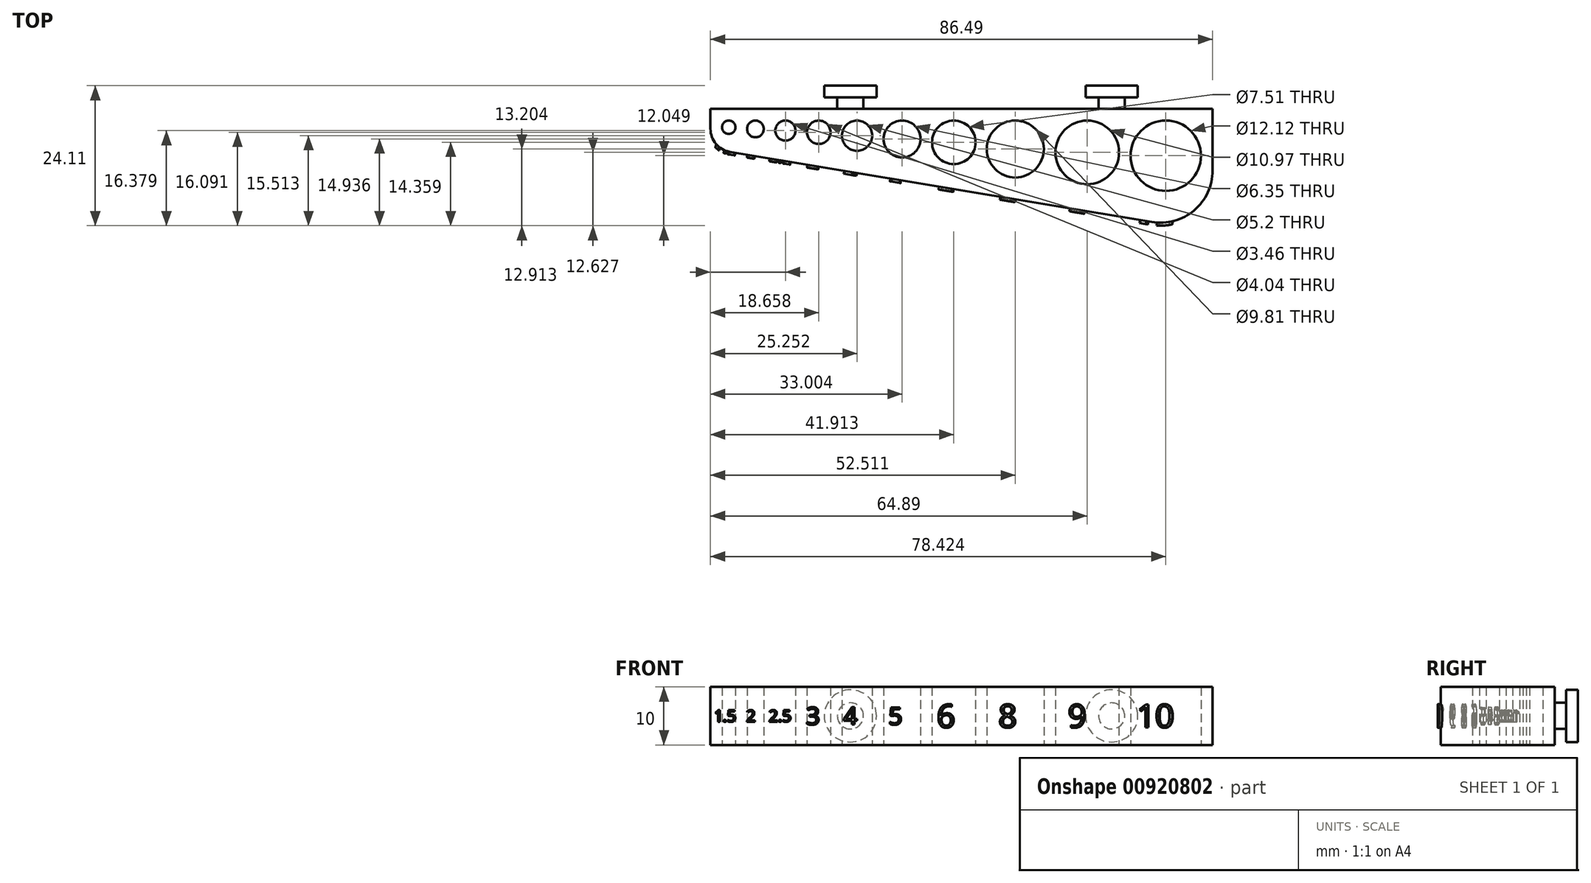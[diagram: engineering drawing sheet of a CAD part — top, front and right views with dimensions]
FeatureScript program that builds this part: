
annotation { "Feature Type Name" : "Feature", "Feature Type Description" : "" }
export const myFeature = defineFeature(function(context is Context, id is Id, definition is map)
    precondition{}
    {
        {
            var Q0;
            Q0=qCreatedBy(makeId("Top.planeOp"),FACE);
            var sketch = newSketch(context, id + "F0", { "sketchPlane" : qUnion([Q0])});
            skCircle(sketch, "E0.cCircle", {"center": v(30.9, 21.07) * mm, "radius": 4.25 * mm, "construction": true});
            skLineSegment(sketch, "E0.0", {"start": v(35.4, 19.12) * mm, "end": v(31.46, 16.2) * mm, "construction": true});
            skLineSegment(sketch, "E0.1", {"start": v(31.46, 16.2) * mm, "end": v(26.96, 18.15) * mm, "construction": true});
            skLineSegment(sketch, "E0.2", {"start": v(26.96, 18.15) * mm, "end": v(26.4, 23.03) * mm, "construction": true});
            skLineSegment(sketch, "E0.3", {"start": v(26.4, 23.03) * mm, "end": v(30.35, 25.95) * mm, "construction": true});
            skLineSegment(sketch, "E0.4", {"start": v(30.35, 25.95) * mm, "end": v(34.85, 24) * mm, "construction": true});
            skLineSegment(sketch, "E0.5", {"start": v(34.85, 24) * mm, "end": v(35.4, 19.12) * mm, "construction": true});
            skPoint(sketch, "E0.0.midPoint", {"position": v(33.43, 17.66) * mm});
            skCircle(sketch, "E1", {"center": v(30.9, 21.07) * mm, "radius": 4.9 * mm});
            skCircle(sketch, "E2.cCircle", {"center": v(-2.95, 23.96) * mm, "radius": 1.75 * mm, "construction": true});
            skLineSegment(sketch, "E2.0", {"start": v(-1.1, 23.15) * mm, "end": v(-2.72, 21.95) * mm, "construction": true});
            skLineSegment(sketch, "E2.1", {"start": v(-2.72, 21.95) * mm, "end": v(-4.58, 22.76) * mm, "construction": true});
            skLineSegment(sketch, "E2.2", {"start": v(-4.58, 22.76) * mm, "end": v(-4.8, 24.77) * mm, "construction": true});
            skLineSegment(sketch, "E2.3", {"start": v(-4.8, 24.77) * mm, "end": v(-3.18, 25.97) * mm, "construction": true});
            skLineSegment(sketch, "E2.4", {"start": v(-3.18, 25.97) * mm, "end": v(-1.33, 25.16) * mm, "construction": true});
            skLineSegment(sketch, "E2.5", {"start": v(-1.33, 25.16) * mm, "end": v(-1.1, 23.15) * mm, "construction": true});
            skPoint(sketch, "E2.0.midPoint", {"position": v(-1.91, 22.55) * mm});
            skCircle(sketch, "E3", {"center": v(-2.95, 23.96) * mm, "radius": 2.02 * mm});
            skCircle(sketch, "E4.cCircle", {"center": v(-8.7, 24.25) * mm, "radius": 1.5 * mm, "construction": true});
            skLineSegment(sketch, "E4.0", {"start": v(-7.1, 23.56) * mm, "end": v(-8.5, 22.53) * mm, "construction": true});
            skLineSegment(sketch, "E4.1", {"start": v(-8.5, 22.53) * mm, "end": v(-10.09, 23.22) * mm, "construction": true});
            skLineSegment(sketch, "E4.2", {"start": v(-10.09, 23.22) * mm, "end": v(-10.29, 24.94) * mm, "construction": true});
            skLineSegment(sketch, "E4.3", {"start": v(-10.29, 24.94) * mm, "end": v(-8.9, 25.97) * mm, "construction": true});
            skLineSegment(sketch, "E4.4", {"start": v(-8.9, 25.97) * mm, "end": v(-7.3, 25.28) * mm, "construction": true});
            skLineSegment(sketch, "E4.5", {"start": v(-7.3, 25.28) * mm, "end": v(-7.1, 23.56) * mm, "construction": true});
            skPoint(sketch, "E4.0.midPoint", {"position": v(-7.8, 23.04) * mm});
            skCircle(sketch, "E5", {"center": v(-8.7, 24.25) * mm, "radius": 1.73 * mm});
            skCircle(sketch, "E6.cCircle", {"center": v(-18.45, 24.83) * mm, "radius": 1 * mm, "construction": true});
            skLineSegment(sketch, "E6.0", {"start": v(-17.7, 23.95) * mm, "end": v(-18.84, 23.74) * mm, "construction": true});
            skLineSegment(sketch, "E6.1", {"start": v(-18.84, 23.74) * mm, "end": v(-19.59, 24.61) * mm, "construction": true});
            skLineSegment(sketch, "E6.2", {"start": v(-19.59, 24.61) * mm, "end": v(-19.2, 25.7) * mm, "construction": true});
            skLineSegment(sketch, "E6.3", {"start": v(-19.2, 25.7) * mm, "end": v(-18.07, 25.92) * mm, "construction": true});
            skLineSegment(sketch, "E6.4", {"start": v(-18.07, 25.92) * mm, "end": v(-17.32, 25.04) * mm, "construction": true});
            skLineSegment(sketch, "E6.5", {"start": v(-17.32, 25.04) * mm, "end": v(-17.7, 23.95) * mm, "construction": true});
            skPoint(sketch, "E6.0.midPoint", {"position": v(-18.27, 23.84) * mm});
            skCircle(sketch, "E7", {"center": v(-18.45, 24.83) * mm, "radius": 1.15 * mm});
            skCircle(sketch, "E8.cCircle", {"center": v(3.64, 23.38) * mm, "radius": 2.25 * mm, "construction": true});
            skLineSegment(sketch, "E8.0", {"start": v(6.02, 22.35) * mm, "end": v(3.94, 20.8) * mm, "construction": true});
            skLineSegment(sketch, "E8.1", {"start": v(3.94, 20.8) * mm, "end": v(1.55, 21.84) * mm, "construction": true});
            skLineSegment(sketch, "E8.2", {"start": v(1.55, 21.84) * mm, "end": v(1.26, 24.42) * mm, "construction": true});
            skLineSegment(sketch, "E8.3", {"start": v(1.26, 24.42) * mm, "end": v(3.35, 25.96) * mm, "construction": true});
            skLineSegment(sketch, "E8.4", {"start": v(3.35, 25.96) * mm, "end": v(5.73, 24.93) * mm, "construction": true});
            skLineSegment(sketch, "E8.5", {"start": v(5.73, 24.93) * mm, "end": v(6.02, 22.35) * mm, "construction": true});
            skPoint(sketch, "E8.0.midPoint", {"position": v(4.98, 21.57) * mm});
            skCircle(sketch, "E9", {"center": v(3.64, 23.38) * mm, "radius": 2.6 * mm});
            skCircle(sketch, "E10.cCircle", {"center": v(11.4, 22.8) * mm, "radius": 2.75 * mm, "construction": true});
            skLineSegment(sketch, "E10.0", {"start": v(14.3, 21.54) * mm, "end": v(11.75, 19.65) * mm, "construction": true});
            skLineSegment(sketch, "E10.1", {"start": v(11.75, 19.65) * mm, "end": v(8.84, 20.92) * mm, "construction": true});
            skLineSegment(sketch, "E10.2", {"start": v(8.84, 20.92) * mm, "end": v(8.48, 24.07) * mm, "construction": true});
            skLineSegment(sketch, "E10.3", {"start": v(8.48, 24.07) * mm, "end": v(11.03, 25.96) * mm, "construction": true});
            skLineSegment(sketch, "E10.4", {"start": v(11.03, 25.96) * mm, "end": v(13.95, 24.7) * mm, "construction": true});
            skLineSegment(sketch, "E10.5", {"start": v(13.95, 24.7) * mm, "end": v(14.3, 21.54) * mm, "construction": true});
            skPoint(sketch, "E10.0.midPoint", {"position": v(13.03, 20.6) * mm});
            skCircle(sketch, "E11", {"center": v(11.4, 22.8) * mm, "radius": 3.18 * mm});
            skCircle(sketch, "E12.cCircle", {"center": v(43.28, 20.5) * mm, "radius": 4.75 * mm, "construction": true});
            skLineSegment(sketch, "E12.0", {"start": v(48.3, 18.3) * mm, "end": v(43.9, 15.05) * mm, "construction": true});
            skLineSegment(sketch, "E12.1", {"start": v(43.9, 15.05) * mm, "end": v(38.87, 17.23) * mm, "construction": true});
            skLineSegment(sketch, "E12.2", {"start": v(38.87, 17.23) * mm, "end": v(38.25, 22.68) * mm, "construction": true});
            skLineSegment(sketch, "E12.3", {"start": v(38.25, 22.68) * mm, "end": v(42.66, 25.95) * mm, "construction": true});
            skLineSegment(sketch, "E12.4", {"start": v(42.66, 25.95) * mm, "end": v(47.69, 23.76) * mm, "construction": true});
            skLineSegment(sketch, "E12.5", {"start": v(47.69, 23.76) * mm, "end": v(48.3, 18.3) * mm, "construction": true});
            skPoint(sketch, "E12.0.midPoint", {"position": v(46.1, 16.68) * mm});
            skCircle(sketch, "E13", {"center": v(43.28, 20.5) * mm, "radius": 5.48 * mm});
            skCircle(sketch, "E14.cCircle", {"center": v(56.81, 19.92) * mm, "radius": 5.25 * mm, "construction": true});
            skLineSegment(sketch, "E14.0", {"start": v(62.37, 17.5) * mm, "end": v(57.5, 13.9) * mm, "construction": true});
            skLineSegment(sketch, "E14.1", {"start": v(57.5, 13.9) * mm, "end": v(51.94, 16.31) * mm, "construction": true});
            skLineSegment(sketch, "E14.2", {"start": v(51.94, 16.31) * mm, "end": v(51.25, 22.34) * mm, "construction": true});
            skLineSegment(sketch, "E14.3", {"start": v(51.25, 22.34) * mm, "end": v(56.13, 25.94) * mm, "construction": true});
            skLineSegment(sketch, "E14.4", {"start": v(56.13, 25.94) * mm, "end": v(61.69, 23.53) * mm, "construction": true});
            skLineSegment(sketch, "E14.5", {"start": v(61.69, 23.53) * mm, "end": v(62.37, 17.5) * mm, "construction": true});
            skPoint(sketch, "E14.0.midPoint", {"position": v(59.94, 15.7) * mm});
            skCircle(sketch, "E15", {"center": v(56.81, 19.92) * mm, "radius": 6.06 * mm});
            skCircle(sketch, "E16.cCircle", {"center": v(20.3, 22.23) * mm, "radius": 3.25 * mm, "construction": true});
            skLineSegment(sketch, "E16.0", {"start": v(23.74, 20.73) * mm, "end": v(20.73, 18.5) * mm, "construction": true});
            skLineSegment(sketch, "E16.1", {"start": v(20.73, 18.5) * mm, "end": v(17.29, 20) * mm, "construction": true});
            skLineSegment(sketch, "E16.2", {"start": v(17.29, 20) * mm, "end": v(16.86, 23.72) * mm, "construction": true});
            skLineSegment(sketch, "E16.3", {"start": v(16.86, 23.72) * mm, "end": v(19.88, 25.96) * mm, "construction": true});
            skLineSegment(sketch, "E16.4", {"start": v(19.88, 25.96) * mm, "end": v(23.32, 24.46) * mm, "construction": true});
            skLineSegment(sketch, "E16.5", {"start": v(23.32, 24.46) * mm, "end": v(23.74, 20.73) * mm, "construction": true});
            skPoint(sketch, "E16.0.midPoint", {"position": v(22.24, 19.62) * mm});
            skCircle(sketch, "E17", {"center": v(20.3, 22.23) * mm, "radius": 3.75 * mm});
            skLineSegment(sketch, "E18.bottom", {"start": v(64.88, 27.98) * mm, "end": v(-21.6, 27.98) * mm});
            skLineSegment(sketch, "E18.top", {"start": v(64.88, 7.98) * mm, "end": v(57.46, 7.98) * mm});
            skLineSegment(sketch, "E18.left", {"start": v(64.88, 27.98) * mm, "end": v(64.88, 7.98) * mm});
            skLineSegment(sketch, "E18.right", {"start": v(-21.6, 27.98) * mm, "end": v(-21.6, 21.17) * mm});
            skLineSegment(sketch, "E19", {"start": v(64.88, 25.98) * mm, "end": v(-21.6, 25.98) * mm, "construction": true});
            skCircle(sketch, "E20.cCircle", {"center": v(-13.86, 24.54) * mm, "radius": 1.25 * mm, "construction": true});
            skLineSegment(sketch, "E20.0", {"start": v(-12.54, 23.96) * mm, "end": v(-13.7, 23.1) * mm, "construction": true});
            skLineSegment(sketch, "E20.1", {"start": v(-13.7, 23.1) * mm, "end": v(-15.02, 23.68) * mm, "construction": true});
            skLineSegment(sketch, "E20.2", {"start": v(-15.02, 23.68) * mm, "end": v(-15.19, 25.11) * mm, "construction": true});
            skLineSegment(sketch, "E20.3", {"start": v(-15.19, 25.11) * mm, "end": v(-14.03, 25.97) * mm, "construction": true});
            skLineSegment(sketch, "E20.4", {"start": v(-14.03, 25.97) * mm, "end": v(-12.7, 25.4) * mm, "construction": true});
            skLineSegment(sketch, "E20.5", {"start": v(-12.7, 25.4) * mm, "end": v(-12.54, 23.96) * mm, "construction": true});
            skPoint(sketch, "E20.0.midPoint", {"position": v(-13.12, 23.53) * mm});
            skCircle(sketch, "E21", {"center": v(-13.86, 24.54) * mm, "radius": 1.44 * mm});
            skLineSegment(sketch, "E22", {"start": v(57.46, 7.98) * mm, "end": v(-21.6, 21.17) * mm});
            skSolve(sketch);
        }
        {
            var Q0;
            Q0=makeQuery(id+"F0.imprint","IMPRINT",FACE,{"disambiguationData":[TD([[makeQuery(id+"F0.imprint","IMPRINT",EDGE,{"derivedFrom":sQuery(id+"F0.wireOp",EDGE,"E1")}),-1.0]])]});
            extrude(context, id + "F1", {"entities" : qUnion([Q0]), "depth" : 10 * mm, "offsetDistance" : 25 * mm});
        }
        {
            var Q0;
            Q0=makeQuery(id+"F1.opExtrude","SWEPT_EDGE",EDGE,{"disambiguationData":[OSD([sQuery(id+"F0.wireOp",EDGE,"E18.top"),sQuery(id+"F0.wireOp",EDGE,"E18.left")])]});
            fillet(context, id + "F2", {"entities" : qUnion([Q0]), "radius" : 8 * mm, "tangentPropagation" : true, "allowEdgeOverflow" : false});
        }
        {
            var Q0;
            Q0=makeQuery(id+"F2.opFillet","BLEND_EDGE",EDGE,{"blendedFrom":[makeQuery(id+"F1.opExtrude","SWEPT_EDGE",EDGE,{"disambiguationData":[OSD([sQuery(id+"F0.wireOp",EDGE,"E18.top"),sQuery(id+"F0.wireOp",EDGE,"E18.left")])]}),makeQuery(id+"F1.opExtrude","SWEPT_FACE",FACE,{"disambiguationData":[OSD([sQuery(id+"F0.wireOp",EDGE,"E22")])]})],"blendedInto":[makeQuery(id+"F1.opExtrude","SWEPT_FACE",FACE,{"disambiguationData":[OSD([sQuery(id+"F0.wireOp",EDGE,"E22")])]})]});
            fillet(context, id + "F3", {"entities" : qUnion([Q0]), "radius" : 9 * mm, "tangentPropagation" : true, "allowEdgeOverflow" : false});
        }
        {
            var Q0;
            Q0=makeQuery(id+"F1.opExtrude","SWEPT_EDGE",EDGE,{"disambiguationData":[OSD([sQuery(id+"F0.wireOp",EDGE,"E18.right"),sQuery(id+"F0.wireOp",EDGE,"E22")])]});
            fillet(context, id + "F4", {"entities" : qUnion([Q0]), "radius" : 4 * mm, "tangentPropagation" : true, "allowEdgeOverflow" : false});
        }
        {
            var Q0;
            Q0=makeQuery(id+"F1.opExtrude","SWEPT_FACE",FACE,{"disambiguationData":[OSD([sQuery(id+"F0.wireOp",EDGE,"E22")])]});
            var sketch = newSketch(context, id + "F5", { "sketchPlane" : qUnion([Q0])});
            skText(sketch, "E23", { "text": "10", "fontName": "OpenSans-Regular.ttf"});
            skText(sketch, "E24", { "text": "9\n", "fontName": "OpenSans-Regular.ttf"});
            skText(sketch, "E25", { "text": "8\n", "fontName": "OpenSans-Regular.ttf"});
            skText(sketch, "E26", { "text": "6", "fontName": "OpenSans-Regular.ttf"});
            skText(sketch, "E27", { "text": "5", "fontName": "OpenSans-Regular.ttf"});
            skText(sketch, "E28", { "text": "4", "fontName": "OpenSans-Regular.ttf"});
            skText(sketch, "E29", { "text": "3\n", "fontName": "OpenSans-Regular.ttf"});
            skText(sketch, "E30", { "text": "2.5", "fontName": "OpenSans-Regular.ttf"});
            skText(sketch, "E31", { "text": "2", "fontName": "OpenSans-Regular.ttf"});
            skText(sketch, "E32", { "text": "1.5", "fontName": "OpenSans-Regular.ttf"});
            skPoint(sketch, "E32.secondSnap0", {"position": v(-21.4, 4) * mm});
            skLineSegment(sketch, "E33", {"start": v(52.26, 5) * mm, "end": v(-21.4, 5) * mm, "construction": true});
            const initialGuessF5  = {"E23": [0.04972, 0.003, 1, 0, 0.004], "E24": [0.03768, 0.003, 1, 0, 0.004], "E25": [0.02555, 0.003, 1, 0, 0.004], "E26": [0.01477, 0.003, 1, 0, 0.004], "E27": [0.00635, 0.0035, 1, 0, 0.003], "E28": [-0.00152, 0.0035, 1, 0, 0.003], "E29": [-0.00804, 0.0035, 1, 0, 0.003], "E30": [-0.01456, 0.004, 1, 0, 0.002], "E31": [-0.01848, 0.004, 1, 0, 0.002], "E32": [-0.02421, 0.004, 1, 0, 0.002]};
            skSetInitialGuess(sketch, initialGuessF5);
            skSolve(sketch);
        }
        {
            var Q0;
            Q0 = qSketchRegion(id + "F5", true);
            extrude(context, id + "F6", {"entities" : qUnion([Q0]), "operationType" : NewBodyOperationType.ADD, "depth" : 0.5 * mm, "offsetDistance" : 25 * mm, "hasSecondDirection" : true, "secondDirectionOppositeDirection" : true, "secondDirectionDepth" : 1 * mm});
        }
        {
            var Q0;
            Q0=makeQuery(id+"F1.opExtrude","CAP_FACE",FACE,{"disambiguationData":[OSD([sQuery(id+"F0.wireOp",EDGE,"E1"),sQuery(id+"F0.wireOp",EDGE,"E3"),sQuery(id+"F0.wireOp",EDGE,"E5"),sQuery(id+"F0.wireOp",EDGE,"E7"),sQuery(id+"F0.wireOp",EDGE,"E9"),sQuery(id+"F0.wireOp",EDGE,"E11"),sQuery(id+"F0.wireOp",EDGE,"E13"),sQuery(id+"F0.wireOp",EDGE,"E15"),sQuery(id+"F0.wireOp",EDGE,"E17"),sQuery(id+"F0.wireOp",EDGE,"E18.bottom"),sQuery(id+"F0.wireOp",EDGE,"E18.top"),sQuery(id+"F0.wireOp",EDGE,"E18.left"),sQuery(id+"F0.wireOp",EDGE,"E18.right"),sQuery(id+"F0.wireOp",EDGE,"E21"),sQuery(id+"F0.wireOp",EDGE,"E22")])],"isStart":false});
            var sketch = newSketch(context, id + "F7", { "sketchPlane" : qUnion([Q0])});
            skArc(sketch, "E34", {"start": v(-21.06, 22.53) * mm, "mid": v(-19.88, 21.26) * mm, "end": v(-18.27, 20.61) * mm, "construction": true});
            skArc(sketch, "E35", {"start": v(54.4, 8.5) * mm, "mid": v(57.28, 8.48) * mm, "end": v(60.02, 9.38) * mm, "construction": true});
            skArc(sketch, "E36.0", {"start": v(-21.5, 22.28) * mm, "mid": v(-20.16, 20.85) * mm, "end": v(-18.35, 20.12) * mm});
            skArc(sketch, "E37.0", {"start": v(54.31, 8) * mm, "mid": v(57.36, 7.99) * mm, "end": v(60.25, 8.93) * mm});
            skArc(sketch, "E38", {"start": v(54.31, 8) * mm, "mid": v(57.73, 5.62) * mm, "end": v(60.25, 8.93) * mm});
            skArc(sketch, "E39", {"start": v(-21.5, 22.28) * mm, "mid": v(-21.45, 18.97) * mm, "end": v(-18.35, 20.12) * mm});
            skSolve(sketch);
        }
        {
            var Q0;
            Q0 = qSketchRegion(id + "F7", true);
            extrude(context, id + "F8", {"entities" : qUnion([Q0]), "operationType" : NewBodyOperationType.REMOVE, "oppositeDirection" : true, "depth" : 25 * mm, "offsetDistance" : 25 * mm});
        }
        {
            var Q0;
            Q0=makeQuery(id+"F1.opExtrude","SWEPT_FACE",FACE,{"disambiguationData":[OSD([sQuery(id+"F0.wireOp",EDGE,"E18.bottom")])]});
            var sketch = newSketch(context, id + "F9", { "sketchPlane" : qUnion([Q0])});
            skLineSegment(sketch, "E40", {"start": v(-64.88, 10) * mm, "end": v(-64.88, 0) * mm, "construction": true});
            skLineSegment(sketch, "E41", {"start": v(-64.88, 0) * mm, "end": v(21.6, 0) * mm, "construction": true});
            skLineSegment(sketch, "E42", {"start": v(-64.88, 5) * mm, "end": v(21.6, 5) * mm, "construction": true});
            skCircle(sketch, "E43", {"center": v(-47.5, 5) * mm, "radius": 2.25 * mm});
            skCircle(sketch, "E44", {"center": v(-2.5, 5) * mm, "radius": 2.25 * mm});
            skSolve(sketch);
        }
        {
            var Q0;
            Q0 = qSketchRegion(id + "F9", true);
            extrude(context, id + "F10", {"entities" : qUnion([Q0]), "operationType" : NewBodyOperationType.ADD, "depth" : 2 * mm, "offsetDistance" : 25 * mm});
        }
        {
            var Q0;
            Q0=makeQuery(id+"F10.opExtrude","CAP_FACE",FACE,{"disambiguationData":[OSD([sQuery(id+"F9.wireOp",EDGE,"E44")])],"isStart":false});
            var sketch = newSketch(context, id + "F11", { "sketchPlane" : qUnion([Q0])});
            skCircle(sketch, "E45", {"center": v(-47.5, 5) * mm, "radius": 4.5 * mm});
            skCircle(sketch, "E46", {"center": v(-2.5, 5) * mm, "radius": 4.5 * mm});
            skSolve(sketch);
        }
        {
            var Q0;
            Q0 = qSketchRegion(id + "F11", true);
            extrude(context, id + "F12", {"entities" : qUnion([Q0]), "operationType" : NewBodyOperationType.ADD, "depth" : 2 * mm, "offsetDistance" : 25 * mm});
        }
    });
